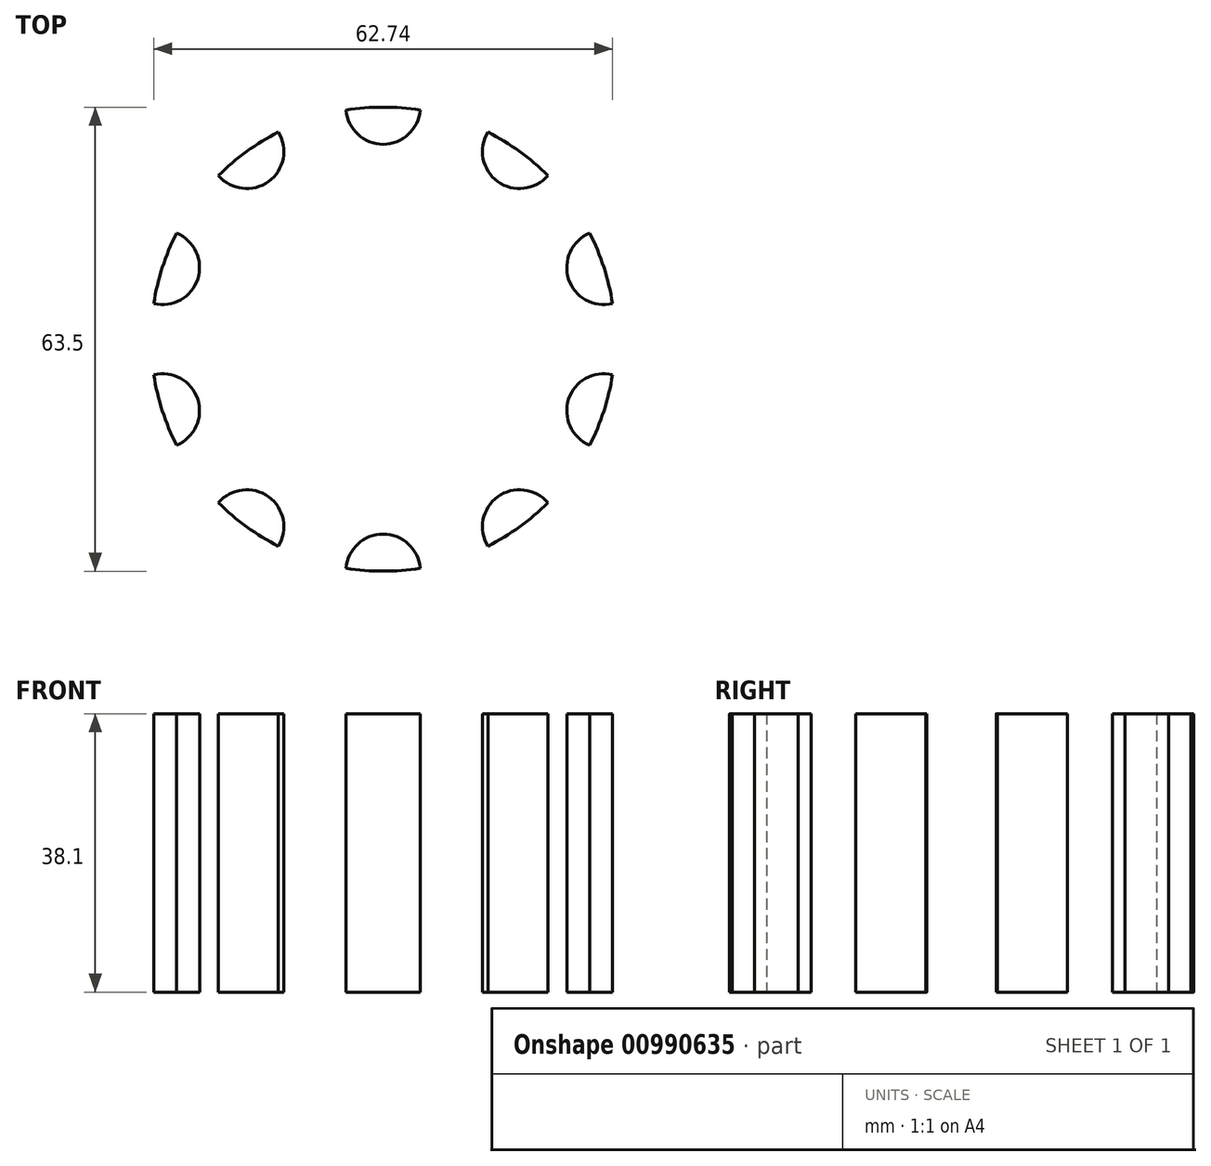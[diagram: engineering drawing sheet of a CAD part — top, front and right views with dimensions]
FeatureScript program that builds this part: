
annotation { "Feature Type Name" : "Feature", "Feature Type Description" : "" }
export const myFeature = defineFeature(function(context is Context, id is Id, definition is map)
    precondition{}
    {
        {
            var Q0;
            Q0=qCreatedBy(makeId("Top.planeOp"),FACE);
            var sketch = newSketch(context, id + "F0", { "sketchPlane" : qUnion([Q0])});
            skCircle(sketch, "E0", {"center": v(0, 0) * mm, "radius": 31.75 * mm});
            skSolve(sketch);
        }
        {
            var Q0;
            Q0=makeQuery(id+"F0.imprint","IMPRINT",FACE,{"disambiguationData":[TD([[makeQuery(id+"F0.imprint","IMPRINT",EDGE,{"derivedFrom":sQuery(id+"F0.wireOp",EDGE,"E0")}),1.0]])]});
            extrude(context, id + "F1", {"entities" : qUnion([Q0]), "depth" : 38.1 * mm});
        }
        {
            var Q0;
            Q0=qCreatedBy(makeId("Top.planeOp"),FACE);
            var sketch = newSketch(context, id + "F2", { "sketchPlane" : qUnion([Q0])});
            skCircle(sketch, "E1", {"center": v(0, 31.75) * mm, "radius": 5.08 * mm});
            skCircle(sketch, "E2.1.0", {"center": v(-18.66, 25.69) * mm, "radius": 5.08 * mm});
            skCircle(sketch, "E2.2.0", {"center": v(-30.2, 9.81) * mm, "radius": 5.08 * mm});
            skCircle(sketch, "E2.3.0", {"center": v(-30.2, -9.81) * mm, "radius": 5.08 * mm});
            skCircle(sketch, "E2.4.0", {"center": v(-18.66, -25.69) * mm, "radius": 5.08 * mm});
            skCircle(sketch, "E2.5.0", {"center": v(0, -31.75) * mm, "radius": 5.08 * mm});
            skCircle(sketch, "E2.6.0", {"center": v(18.66, -25.69) * mm, "radius": 5.08 * mm});
            skCircle(sketch, "E2.7.0", {"center": v(30.2, -9.81) * mm, "radius": 5.08 * mm});
            skCircle(sketch, "E2.8.0", {"center": v(30.2, 9.81) * mm, "radius": 5.08 * mm});
            skCircle(sketch, "E2.9.0", {"center": v(18.66, 25.69) * mm, "radius": 5.08 * mm});
            skPoint(sketch, "E2.center", {"position": v(0, 0) * mm});
            skSolve(sketch);
        }
        {
            var Q0;
            Q0=qSketchRegion(id+"F2",true);
            extrude(context, id + "F3", {"entities" : qUnion([Q0]), "depth" : 50.8 * mm});
        }
        {
            var Q0;
            Q0=makeQuery(id+"F3.opExtrude","SWEPT_BODY",BODY,{"disambiguationData":[OSD([sQuery(id+"F2.wireOp",EDGE,"E2.9.0")])]});
            var Q1;
            Q1=makeQuery(id+"F1.opExtrude","SWEPT_BODY",BODY,{"disambiguationData":[OSD([sQuery(id+"F0.wireOp",EDGE,"E0")])]});
            booleanBodies(context, id + "F4", {"operationType" : BooleanOperationType.INTERSECTION, "tools" : qUnion([Q0, Q1]), "keepTools" : true});
        }
        {
            var Q0;
            Q0=makeQuery(id+"F3.opExtrude","SWEPT_BODY",BODY,{"disambiguationData":[OSD([sQuery(id+"F2.wireOp",EDGE,"E1")])]});
            var Q1;
            Q1=makeQuery(id+"F1.opExtrude","SWEPT_BODY",BODY,{"disambiguationData":[OSD([sQuery(id+"F0.wireOp",EDGE,"E0")])]});
            booleanBodies(context, id + "F5", {"operationType" : BooleanOperationType.INTERSECTION, "tools" : qUnion([Q0, Q1]), "keepTools" : true});
        }
        {
            var Q0;
            Q0=makeQuery(id+"F3.opExtrude","SWEPT_BODY",BODY,{"disambiguationData":[OSD([sQuery(id+"F2.wireOp",EDGE,"E2.1.0")])]});
            var Q1;
            Q1=makeQuery(id+"F1.opExtrude","SWEPT_BODY",BODY,{"disambiguationData":[OSD([sQuery(id+"F0.wireOp",EDGE,"E0")])]});
            booleanBodies(context, id + "F6", {"operationType" : BooleanOperationType.INTERSECTION, "tools" : qUnion([Q0, Q1]), "keepTools" : true});
        }
        {
            var Q0;
            Q0=makeQuery(id+"F1.opExtrude","SWEPT_BODY",BODY,{"disambiguationData":[OSD([sQuery(id+"F0.wireOp",EDGE,"E0")])]});
            var Q1;
            Q1=makeQuery(id+"F3.opExtrude","SWEPT_BODY",BODY,{"disambiguationData":[OSD([sQuery(id+"F2.wireOp",EDGE,"E2.2.0")])]});
            booleanBodies(context, id + "F7", {"operationType" : BooleanOperationType.INTERSECTION, "tools" : qUnion([Q0, Q1]), "keepTools" : true});
        }
        {
            var Q0;
            Q0=makeQuery(id+"F3.opExtrude","SWEPT_BODY",BODY,{"disambiguationData":[OSD([sQuery(id+"F2.wireOp",EDGE,"E2.3.0")])]});
            var Q1;
            Q1=makeQuery(id+"F1.opExtrude","SWEPT_BODY",BODY,{"disambiguationData":[OSD([sQuery(id+"F0.wireOp",EDGE,"E0")])]});
            booleanBodies(context, id + "F8", {"operationType" : BooleanOperationType.INTERSECTION, "tools" : qUnion([Q0, Q1]), "keepTools" : true});
        }
        {
            var Q0;
            Q0=makeQuery(id+"F3.opExtrude","SWEPT_BODY",BODY,{"disambiguationData":[OSD([sQuery(id+"F2.wireOp",EDGE,"E2.4.0")])]});
            var Q1;
            Q1=makeQuery(id+"F1.opExtrude","SWEPT_BODY",BODY,{"disambiguationData":[OSD([sQuery(id+"F0.wireOp",EDGE,"E0")])]});
            booleanBodies(context, id + "F9", {"operationType" : BooleanOperationType.INTERSECTION, "tools" : qUnion([Q0, Q1]), "keepTools" : true});
        }
        {
            var Q0;
            Q0=makeQuery(id+"F3.opExtrude","SWEPT_BODY",BODY,{"disambiguationData":[OSD([sQuery(id+"F2.wireOp",EDGE,"E2.5.0")])]});
            var Q1;
            Q1=makeQuery(id+"F1.opExtrude","SWEPT_BODY",BODY,{"disambiguationData":[OSD([sQuery(id+"F0.wireOp",EDGE,"E0")])]});
            booleanBodies(context, id + "F10", {"operationType" : BooleanOperationType.INTERSECTION, "tools" : qUnion([Q0, Q1]), "keepTools" : true});
        }
        {
            var Q0;
            Q0=makeQuery(id+"F3.opExtrude","SWEPT_BODY",BODY,{"disambiguationData":[OSD([sQuery(id+"F2.wireOp",EDGE,"E2.6.0")])]});
            var Q1;
            Q1=makeQuery(id+"F1.opExtrude","SWEPT_BODY",BODY,{"disambiguationData":[OSD([sQuery(id+"F0.wireOp",EDGE,"E0")])]});
            booleanBodies(context, id + "F11", {"operationType" : BooleanOperationType.INTERSECTION, "tools" : qUnion([Q0, Q1]), "keepTools" : true});
        }
        {
            var Q0;
            Q0=makeQuery(id+"F3.opExtrude","SWEPT_BODY",BODY,{"disambiguationData":[OSD([sQuery(id+"F2.wireOp",EDGE,"E2.7.0")])]});
            var Q1;
            Q1=makeQuery(id+"F1.opExtrude","SWEPT_BODY",BODY,{"disambiguationData":[OSD([sQuery(id+"F0.wireOp",EDGE,"E0")])]});
            booleanBodies(context, id + "F12", {"operationType" : BooleanOperationType.INTERSECTION, "tools" : qUnion([Q0, Q1]), "keepTools" : true});
        }
        {
            var Q0;
            Q0=makeQuery(id+"F3.opExtrude","SWEPT_BODY",BODY,{"disambiguationData":[OSD([sQuery(id+"F2.wireOp",EDGE,"E2.8.0")])]});
            var Q1;
            Q1=makeQuery(id+"F1.opExtrude","SWEPT_BODY",BODY,{"disambiguationData":[OSD([sQuery(id+"F0.wireOp",EDGE,"E0")])]});
            booleanBodies(context, id + "F13", {"operationType" : BooleanOperationType.INTERSECTION, "tools" : qUnion([Q0, Q1]), "keepTools" : true});
        }
        {
            var Q0;
            Q0=makeQuery(id+"F1.opExtrude","SWEPT_BODY",BODY,{"disambiguationData":[OSD([sQuery(id+"F0.wireOp",EDGE,"E0")])]});
            var Q1;
            Q1=makeQuery(id+"F3.opExtrude","SWEPT_BODY",BODY,{"disambiguationData":[OSD([sQuery(id+"F2.wireOp",EDGE,"E2.8.0")])]});
            var Q2;
            Q2=makeQuery(id+"F3.opExtrude","SWEPT_BODY",BODY,{"disambiguationData":[OSD([sQuery(id+"F2.wireOp",EDGE,"E2.9.0")])]});
            var Q3;
            Q3=makeQuery(id+"F3.opExtrude","SWEPT_BODY",BODY,{"disambiguationData":[OSD([sQuery(id+"F2.wireOp",EDGE,"E1")])]});
            var Q4;
            Q4=makeQuery(id+"F3.opExtrude","SWEPT_BODY",BODY,{"disambiguationData":[OSD([sQuery(id+"F2.wireOp",EDGE,"E2.1.0")])]});
            var Q5;
            Q5=makeQuery(id+"F3.opExtrude","SWEPT_BODY",BODY,{"disambiguationData":[OSD([sQuery(id+"F2.wireOp",EDGE,"E2.2.0")])]});
            var Q6;
            Q6=makeQuery(id+"F3.opExtrude","SWEPT_BODY",BODY,{"disambiguationData":[OSD([sQuery(id+"F2.wireOp",EDGE,"E2.3.0")])]});
            var Q7;
            Q7=makeQuery(id+"F3.opExtrude","SWEPT_BODY",BODY,{"disambiguationData":[OSD([sQuery(id+"F2.wireOp",EDGE,"E2.4.0")])]});
            var Q8;
            Q8=makeQuery(id+"F3.opExtrude","SWEPT_BODY",BODY,{"disambiguationData":[OSD([sQuery(id+"F2.wireOp",EDGE,"E2.5.0")])]});
            var Q9;
            Q9=makeQuery(id+"F3.opExtrude","SWEPT_BODY",BODY,{"disambiguationData":[OSD([sQuery(id+"F2.wireOp",EDGE,"E2.6.0")])]});
            var Q10;
            Q10=makeQuery(id+"F3.opExtrude","SWEPT_BODY",BODY,{"disambiguationData":[OSD([sQuery(id+"F2.wireOp",EDGE,"E2.7.0")])]});
            booleanBodies(context, id + "F14", {"operationType" : BooleanOperationType.INTERSECTION, "tools" : qUnion([Q0, Q1, Q2, Q3, Q4, Q5, Q6, Q7, Q8, Q9, Q10])});
        }
    });
